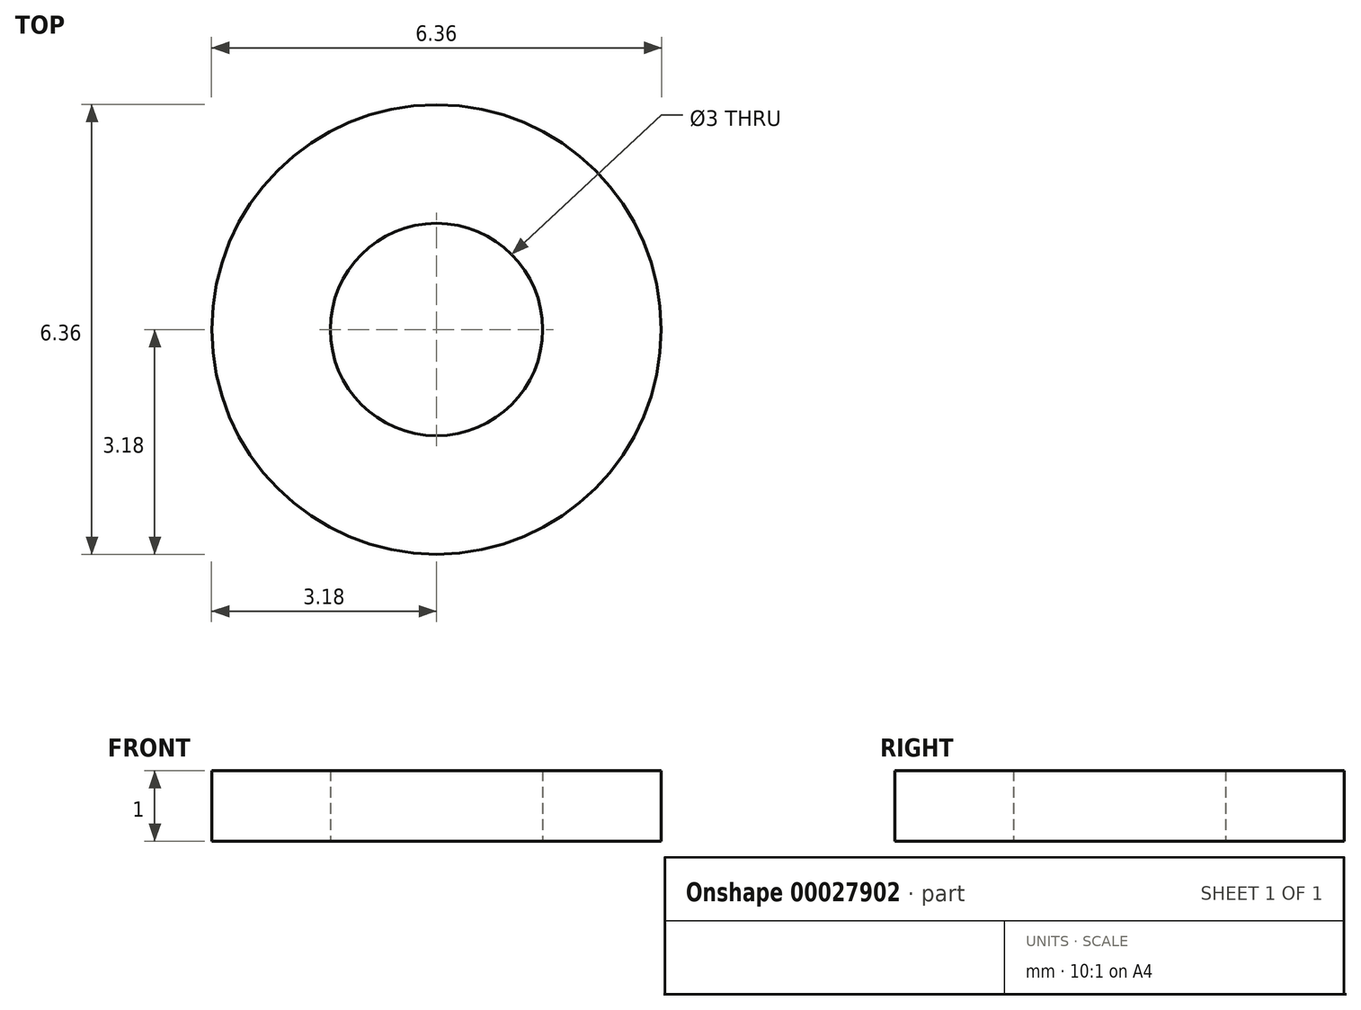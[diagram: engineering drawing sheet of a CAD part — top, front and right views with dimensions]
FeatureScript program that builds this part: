
annotation { "Feature Type Name" : "Feature", "Feature Type Description" : "" }
export const myFeature = defineFeature(function(context is Context, id is Id, definition is map)
    precondition{}
    {
        {
            var Q0;
            Q0=qCreatedBy(makeId("Top.planeOp"),FACE);
            var sketch = newSketch(context, id + "F0", { "sketchPlane" : qUnion([Q0])});
            skCircle(sketch, "E0", {"center": v(0, 0) * mm, "radius": 1.5 * mm});
            skCircle(sketch, "E1", {"center": v(0, 0) * mm, "radius": 3.17 * mm});
            skSolve(sketch);
        }
        {
            var Q0;
            Q0 = qSketchRegion(id + "F0", true);
            extrude(context, id + "F1", {"entities" : qUnion([Q0]), "depth" : 1 * mm});
        }
    });
